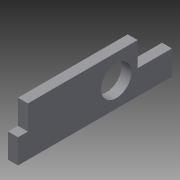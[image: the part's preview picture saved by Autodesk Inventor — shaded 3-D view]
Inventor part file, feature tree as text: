
AUTODESK INVENTOR PART (.ipt)
format: ipt  version: 2013 (Build 170138000, 138)  size: 92,160 bytes
history: native  units: mm
features: extrude x1, sketch x1
ambient origin geometry x8: Origin, YZ Plane, XZ Plane, XY Plane, X Axis, Y Axis, Z Axis, Center Point
feature tree (2):
  extrude  "Extrusion5"  Depth=3.0mm
  sketch  "Sketch1"  dims[d0=3.0mm d2=3.0mm d27=3.25mm d28=8.0mm d29=10.0mm d34=2.0mm d35=8.0mm d36=3.25mm d37=0.0mm d38=36.0mm]
